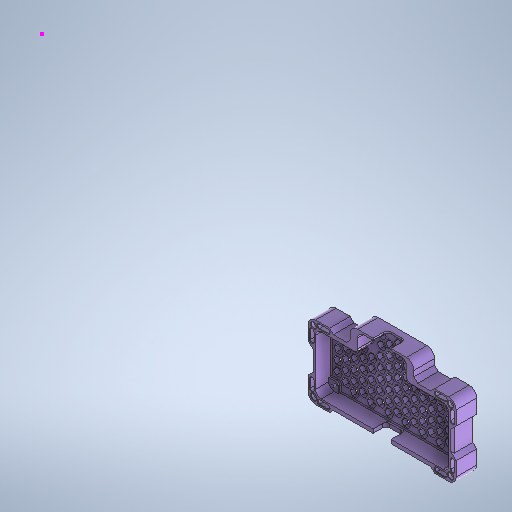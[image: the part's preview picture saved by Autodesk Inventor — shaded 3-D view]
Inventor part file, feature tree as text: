
AUTODESK INVENTOR PART (.ipt)
format: ipt  version: 2025.2 (Build 292293000, 293)  size: 5,417,984 bytes
history: native  units: mm
features: sketch x20, extrude x19, other x4, chamfer x4, fillet x1
ambient origin geometry x8: Origin, YZ Plane, XZ Plane, XY Plane, X Axis, Y Axis, Z Axis, Center Point
bodies: Body1 (feature_tree), Body2 (feature_tree), Body3 (feature_tree), Body4 (feature_tree), Body5 (feature_tree), Body6 (feature_tree), Body7 (feature_tree), Body8 (feature_tree), Body9 (feature_tree), Body10 (feature_tree), Body11 (feature_tree), Body12 (feature_tree), Body13 (feature_tree), Body14 (feature_tree), Body15 (feature_tree), Body16 (feature_tree), Body17 (feature_tree), Body18 (feature_tree), Body19 (feature_tree), Body20 (feature_tree), Body21 (feature_tree), Body22 (feature_tree), Body23 (feature_tree), Body24 (feature_tree), Body25 (feature_tree), Body26 (feature_tree), Body27 (feature_tree), Body28 (feature_tree), Body29 (feature_tree), Body30 (feature_tree), Body31 (feature_tree), Body32 (feature_tree), Body33 (feature_tree), Body34 (feature_tree), Body35 (feature_tree), Body36 (feature_tree), Body37 (feature_tree), Body38 (feature_tree), Body39 (feature_tree), Body40 (feature_tree), Body41 (feature_tree), Body42 (feature_tree), Body43 (feature_tree), Body44 (feature_tree), Body45 (feature_tree), Body46 (feature_tree), Body47 (feature_tree), Body48 (feature_tree), Body49 (feature_tree), Body50 (feature_tree), Body51 (feature_tree), Body52 (feature_tree), Body53 (feature_tree), Body54 (feature_tree), Body55 (feature_tree), Body56 (feature_tree), Body57 (feature_tree), Body58 (feature_tree), Body59 (feature_tree), Body60 (feature_tree), Body61 (feature_tree), Body62 (feature_tree), Body63 (feature_tree), Body64 (feature_tree), Body65 (feature_tree), Body66 (feature_tree), Body67 (feature_tree), Body68 (feature_tree), Body69 (feature_tree), Body70 (feature_tree), Body71 (feature_tree), Body72 (feature_tree), Body73 (feature_tree), Body74 (feature_tree), Body75 (feature_tree), Body76 (feature_tree), Body77 (feature_tree), Body78 (feature_tree), Body79 (feature_tree), Body80 (feature_tree), Body81 (feature_tree), Body82 (feature_tree), Body83 (feature_tree), Body84 (feature_tree), Body85 (feature_tree), Body86 (feature_tree), Body87 (feature_tree), Body88 (feature_tree), Body89 (feature_tree), Body90 (feature_tree), Body91 (feature_tree), Body92 (feature_tree), Body93 (feature_tree), Body94 (feature_tree), Body95 (feature_tree), Body96 (feature_tree), Body97 (feature_tree), Body98 (feature_tree), Body99 (feature_tree), Body100 (feature_tree), Body101 (feature_tree), Body102 (feature_tree), Body103 (feature_tree), Body104 (feature_tree), Body105 (feature_tree), Body106 (feature_tree), Body107 (feature_tree), Body108 (feature_tree), Body109 (feature_tree), Body110 (feature_tree), Body111 (feature_tree), Body112 (feature_tree), Body113 (feature_tree), Body114 (feature_tree), Body115 (feature_tree), Body116 (feature_tree), Body117 (feature_tree), Body118 (feature_tree), Body119 (feature_tree), Body120 (feature_tree), Body121 (feature_tree), Body122 (feature_tree), Body123 (feature_tree), Body124 (feature_tree), Body125 (feature_tree), Body126 (feature_tree), Body127 (feature_tree), Body128 (feature_tree), Body129 (feature_tree), Body130 (feature_tree), Body131 (feature_tree), Body132 (feature_tree), Body133 (feature_tree), Body134 (feature_tree), Body135 (feature_tree), Body136 (feature_tree), Body137 (feature_tree), Body138 (feature_tree), Body139 (feature_tree), Body140 (feature_tree), Body141 (feature_tree), Body142 (feature_tree), Body143 (feature_tree), Body144 (feature_tree), Body145 (feature_tree), Body146 (feature_tree), Body147 (feature_tree), Body148 (feature_tree), Body149 (feature_tree), Body150 (feature_tree), Body151 (feature_tree), Body152 (feature_tree), Body153 (feature_tree), Body154 (feature_tree), Body155 (feature_tree), Body156 (feature_tree), Body157 (feature_tree), Body158 (feature_tree), Body159 (feature_tree), Body160 (feature_tree), Body161 (feature_tree), Body162 (feature_tree), Body163 (feature_tree), Body164 (feature_tree), Body165 (feature_tree), Body166 (feature_tree), Body167 (feature_tree), Body168 (feature_tree), Body169 (feature_tree), Body170 (feature_tree), Body171 (feature_tree), Body172 (feature_tree), Body173 (feature_tree), Body174 (feature_tree), Body175 (feature_tree), Body176 (feature_tree), Body177 (feature_tree), Body178 (feature_tree), Body179 (feature_tree), Body180 (feature_tree), Body181 (feature_tree), Body182 (feature_tree), Body183 (feature_tree), Body184 (feature_tree), Body185 (feature_tree), Body186 (feature_tree), Body187 (feature_tree), Body188 (feature_tree), Body189 (feature_tree), Body190 (feature_tree), Body191 (feature_tree), Body192 (feature_tree), Body193 (feature_tree), Body194 (feature_tree), Body195 (feature_tree), Body196 (feature_tree), Body197 (feature_tree), Body198 (feature_tree), Body199 (feature_tree), Body200 (feature_tree), Body201 (feature_tree), Body202 (feature_tree), Body203 (feature_tree), Body204 (feature_tree), Body205 (feature_tree), Body206 (feature_tree), Body207 (feature_tree), Body208 (feature_tree), Body209 (feature_tree), Body210 (feature_tree), Body211 (feature_tree), Body212 (feature_tree), Body213 (feature_tree), Body214 (feature_tree), Body215 (feature_tree), Body216 (feature_tree), Body217 (feature_tree), Body218 (feature_tree), Body219 (feature_tree), Body220 (feature_tree), Body221 (feature_tree), Body222 (feature_tree), Body223 (feature_tree), Body224 (feature_tree), Body225 (feature_tree), Body226 (feature_tree), Body227 (feature_tree), Body228 (feature_tree), Body229 (feature_tree), Body230 (feature_tree), Body231 (feature_tree), Body232 (feature_tree), Body233 (feature_tree), Body234 (feature_tree), Body235 (feature_tree), Body236 (feature_tree), Body237 (feature_tree), Body238 (feature_tree), Body239 (feature_tree), Body240 (feature_tree), Body241 (feature_tree), Body242 (feature_tree), Body243 (feature_tree), Body244 (feature_tree)
feature tree (48):
  other  "Bryła1"
  sketch  "Szkic1"
  extrude  "Wyciągnięcie proste1"  Depth=4.0mm
  extrude  "Wyciągnięcie proste2"  Depth=3.0mm
  extrude  "Wyciągnięcie proste3"  Depth=3.0mm
  extrude  "Wyciągnięcie proste4"  Depth=2.0mm
  sketch  "Szkic2"
  extrude  "Wyciągnięcie proste5"  Depth=5.0mm
  extrude  "Wyciągnięcie proste7"  Depth=0.8mm TaperAngle=0.0deg
  extrude  "Wyciągnięcie proste8"  Depth=3.65mm TaperAngle=0.0deg
  chamfer  "Faza1"  Distance=6.5mm
  chamfer  "Faza2"  Distance=2.5mm
  sketch  "Szkic5"
  sketch  "Szkic6"
  sketch  "Szkic9"
  extrude  "Wyciągnięcie proste12"  Depth=2.0mm
  sketch  "Szkic12"
  extrude  "Wyciągnięcie proste13"  Depth=2.0mm
  extrude  "Wyciągnięcie proste14"  Depth=2.0mm
  sketch  "Szkic14"
  extrude  "Wyciągnięcie proste15"  Depth=2.0mm
  extrude  "Wyciągnięcie proste16"  Depth=3.0mm
  extrude  "Wyciągnięcie proste17"  Depth=3.0mm
  chamfer  "Faza3"  Distance=3.0mm
  chamfer  "Faza4"  Distance=3.0mm
  other  "Płaszczyzna konstrukcyjna2"
  sketch  "Szkic15"
  extrude  "Wyciągnięcie proste18"  Depth=1.4mm TaperAngle=0.0deg
  sketch  "Szkic17"
  extrude  "Wyciągnięcie proste21"  Depth=0.2mm
  extrude  "Wyciągnięcie proste24"  Depth=0.2mm
  extrude  "Wyciągnięcie proste25"  Depth=0.2mm
  fillet  "Zaokrąglenie1"  Radius=2.0mm
  extrude  "Wyciągnięcie proste26"  Depth=2.0mm
  sketch  "Szkic24"
  sketch  "Szkic25"
  extrude  "Wyciągnięcie proste27"  Depth=6.0mm TaperAngle=0.0deg
  sketch  "Szkic3"
  sketch  "Szkic4"
  sketch  "Szkic11"
  sketch  "Szkic13"
  sketch  "Szkic18"
  sketch  "Szkic21"
  sketch  "Szkic22"
  sketch  "Szkic23"
  sketch  "Szkic26"
  other  "Złożony1"
  other  "Srf1"
